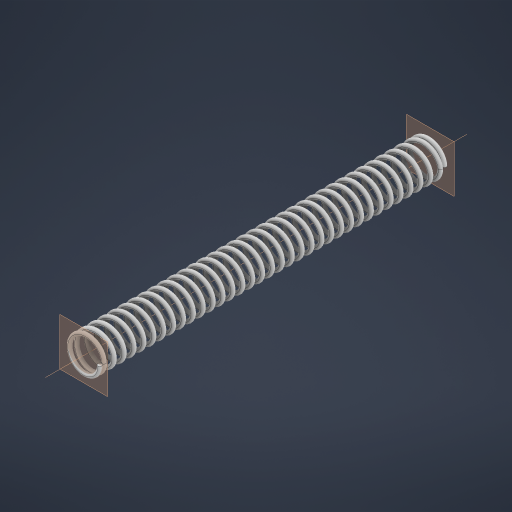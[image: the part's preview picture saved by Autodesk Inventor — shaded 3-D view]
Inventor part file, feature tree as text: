
AUTODESK INVENTOR PART (.ipt)
format: ipt  version: 2024 (Build 280153000, 153)  size: 1,215,488 bytes
history: native  units: in
note: dims shown in document units (in); Inventor stores cm internally (conversion verified against a paired STEP export)
features: plane x1, sweep x1
ambient origin geometry x8: Origin, YZ Plane, XZ Plane, XY Plane, X Axis, Y Axis, Z Axis, Center Point
bodies: Solid1 (feature_tree)
feature tree (2):
  plane  "Work Plane1"
  sweep  "Sweep1"
